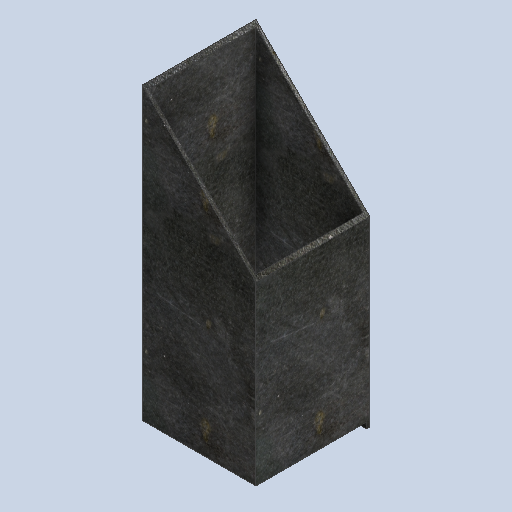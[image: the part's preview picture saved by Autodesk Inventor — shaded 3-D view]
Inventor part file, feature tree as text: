
AUTODESK INVENTOR PART (.ipt)
format: ipt  version: 2024.3 (Build 283343000, 343)  size: 282,112 bytes
history: native  units: mm
features: extrude x3, sketch x3, projected_geometry x2
ambient origin geometry x8: Origin, YZ Plane, XZ Plane, XY Plane, X Axis, Y Axis, Z Axis, Center Point
bodies: Solid1 (feature_tree)
feature tree (8):
  extrude  "Extrusion1"  Depth=3.0mm
  extrude  "Extrusion2"  Depth=100.0mm
  extrude  "Extrusion3"  TaperAngle=45.0deg  [1 undecoded]
  sketch  "Sketch1"  dims[d0=3.0mm d1=3.0mm]
  sketch  "Sketch2"  dims[d2=100.0mm d3=100.0mm]
  projected_geometry  "Projected Loop1"
  sketch  "Sketch3"  dims[d4=255.0mm d5=0.0mm d6=45.0deg d7=0.0mm d8=0.0mm d9=10.0mm d10=3.0mm d11=25.0mm d12=5.0mm d13=0.0mm]
  projected_geometry  "Projected Loop2"
note: 1 required parameter value undecoded (feature->parameter linkage not recoverable at this tier; creation-order binding heuristic only, values carry confidence <= 0.55)
